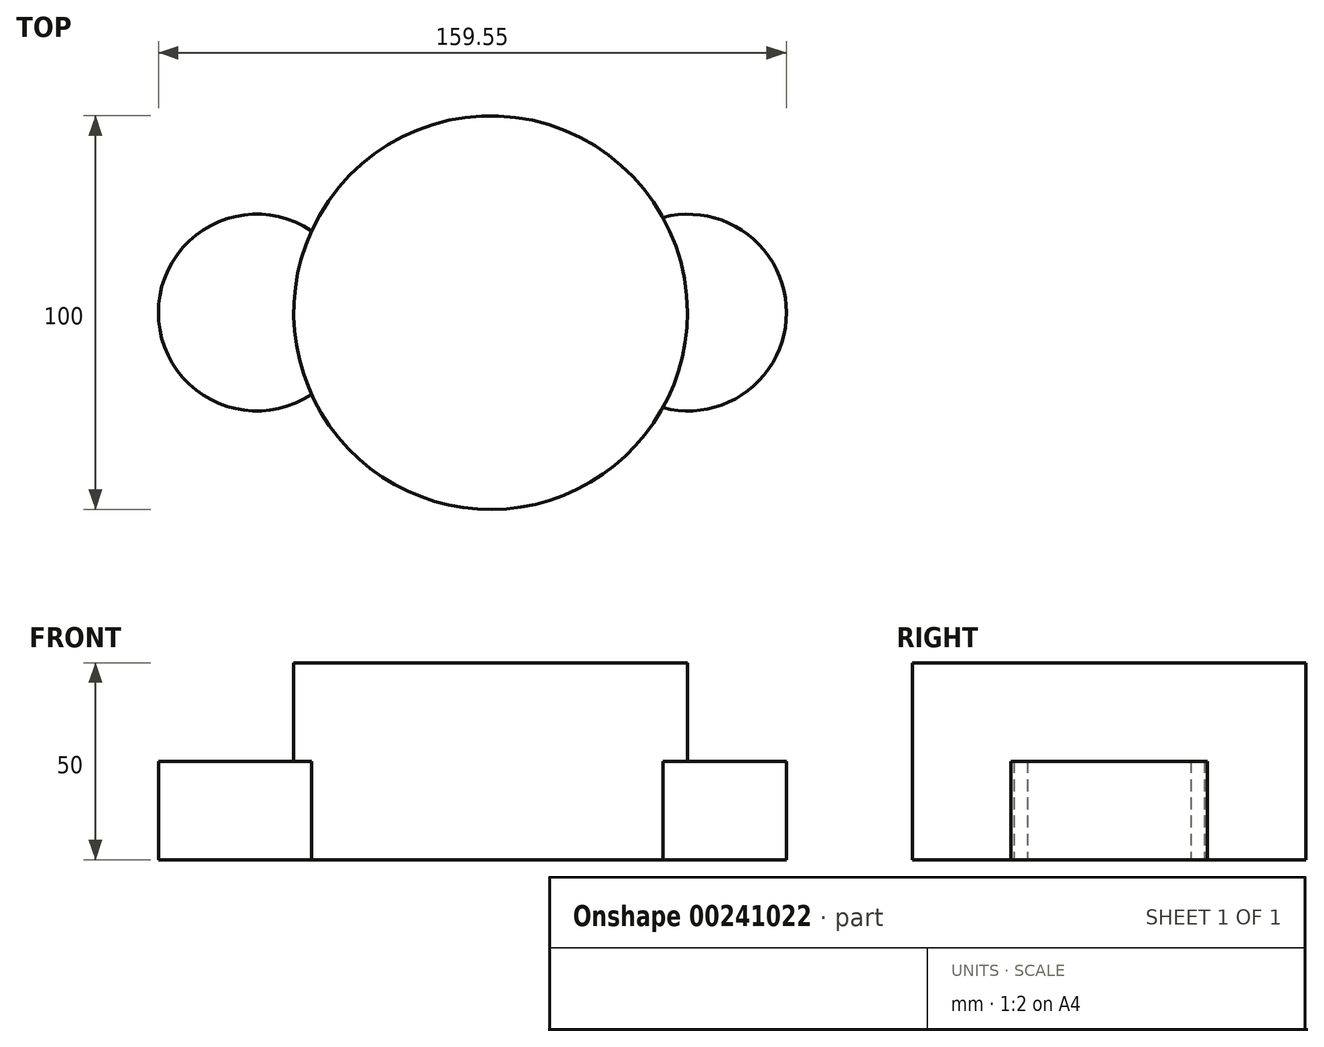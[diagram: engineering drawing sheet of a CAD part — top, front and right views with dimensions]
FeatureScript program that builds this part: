
annotation { "Feature Type Name" : "Feature", "Feature Type Description" : "" }
export const myFeature = defineFeature(function(context is Context, id is Id, definition is map)
    precondition{}
    {
        {
            var Q0;
            Q0=qCreatedBy(makeId("Top.planeOp"),FACE);
            var sketch = newSketch(context, id + "F0", { "sketchPlane" : qUnion([Q0])});
            skCircle(sketch, "E0", {"center": v(0, 0) * mm, "radius": 50 * mm});
            skSolve(sketch);
        }
        {
            var Q0;
            Q0=makeQuery(id+"F0.imprint","IMPRINT",FACE,{"disambiguationData":[TD([[makeQuery(id+"F0.imprint","IMPRINT",EDGE,{"derivedFrom":sQuery(id+"F0.wireOp",EDGE,"E0")}),1.0]])]});
            extrude(context, id + "F1", {"entities" : qUnion([Q0]), "depth" : 50 * mm});
        }
        {
            var Q0;
            Q0=qCreatedBy(makeId("Top.planeOp"),FACE);
            var sketch = newSketch(context, id + "F2", { "sketchPlane" : qUnion([Q0])});
            skCircle(sketch, "E1", {"center": v(50.15, 0) * mm, "radius": 25 * mm});
            skCircle(sketch, "E2", {"center": v(-59.4, 0) * mm, "radius": 25 * mm});
            skSolve(sketch);
        }
        {
            var Q0;
            Q0=makeQuery(id+"F2.imprint","IMPRINT",FACE,{"disambiguationData":[TD([[makeQuery(id+"F2.imprint","IMPRINT",EDGE,{"derivedFrom":sQuery(id+"F2.wireOp",EDGE,"E1")}),1.0]])]});
            var Q1;
            Q1=makeQuery(id+"F2.imprint","IMPRINT",FACE,{"disambiguationData":[TD([[makeQuery(id+"F2.imprint","IMPRINT",EDGE,{"derivedFrom":sQuery(id+"F2.wireOp",EDGE,"E2")}),1.0]])]});
            extrude(context, id + "F3", {"entities" : qUnion([Q0, Q1]), "operationType" : NewBodyOperationType.ADD, "depth" : 25 * mm});
        }
    });
